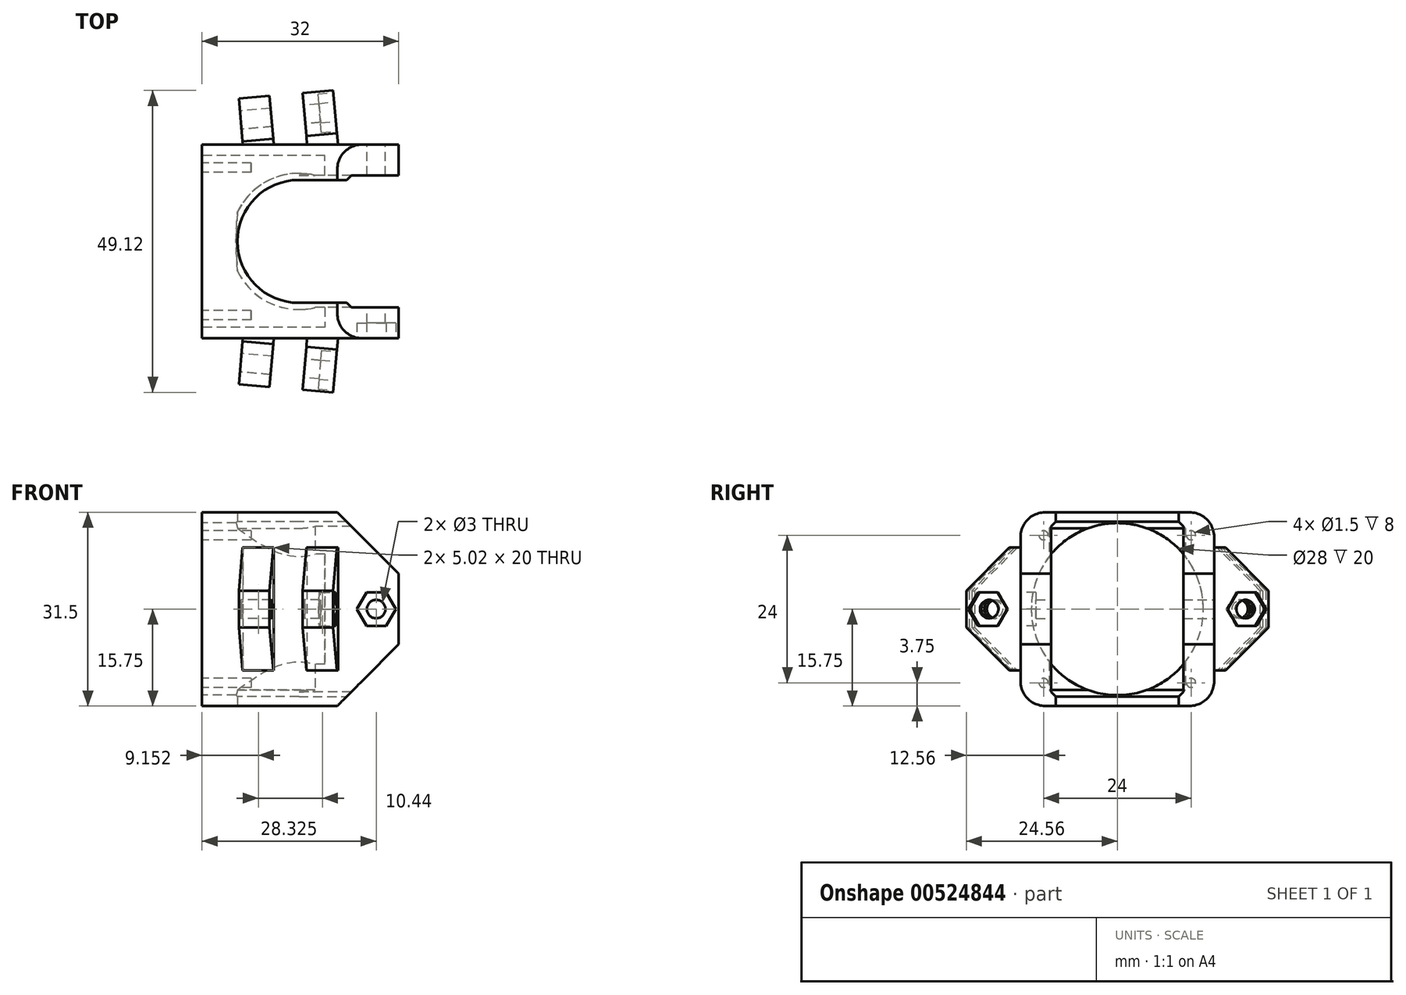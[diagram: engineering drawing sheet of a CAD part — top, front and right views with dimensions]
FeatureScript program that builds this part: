
annotation { "Feature Type Name" : "Feature", "Feature Type Description" : "" }
export const myFeature = defineFeature(function(context is Context, id is Id, definition is map)
    precondition{}
    {
        {
            var Q0;
            Q0=qCreatedBy(makeId("Top.planeOp"),FACE);
            var sketch = newSketch(context, id + "F0", { "sketchPlane" : qUnion([Q0])});
            skLineSegment(sketch, "E0.bottom", {"start": v(-15.75, 15.75) * mm, "end": v(16.25, 15.75) * mm});
            skLineSegment(sketch, "E0.top", {"start": v(-15.75, -15.75) * mm, "end": v(16.25, -15.75) * mm});
            skLineSegment(sketch, "E0.left", {"start": v(-15.75, 15.75) * mm, "end": v(-15.75, -15.75) * mm});
            skLineSegment(sketch, "E0.right", {"start": v(16.25, 15.75) * mm, "end": v(16.25, 10) * mm});
            skArc(sketch, "E1", {"start": v(0, 10) * mm, "mid": v(-10, 0) * mm, "end": v(0, -10) * mm});
            skLineSegment(sketch, "E2", {"start": v(16.25, 10) * mm, "end": v(0, 10) * mm});
            skLineSegment(sketch, "E3", {"start": v(16.25, -10) * mm, "end": v(0, -10) * mm});
            skLineSegment(sketch, "E4.trimOffspring", {"start": v(16.25, -10) * mm, "end": v(16.25, -15.75) * mm});
            skSolve(sketch);
        }
        {
            var Q0;
            Q0=makeQuery(id+"F0.imprint","IMPRINT",FACE,{"disambiguationData":[TD([[makeQuery(id+"F0.imprint","IMPRINT",EDGE,{"derivedFrom":sQuery(id+"F0.wireOp",EDGE,"E0.bottom")}),-1.0]])]});
            extrude(context, id + "F1", {"entities" : qUnion([Q0]), "depth" : (31.5 / 2) * mm, "offsetDistance" : 25 * mm, "hasSecondDirection" : true, "secondDirectionOppositeDirection" : true, "secondDirectionDepth" : (31.5 / 2) * mm});
        }
        {
            var Q0;
            Q0=makeQuery(id+"F1.opExtrude","CAP_EDGE",EDGE,{"disambiguationData":[OSD([sQuery(id+"F0.wireOp",EDGE,"E0.top")])],"isStart":false});
            fillet(context, id + "F2", {"entities" : qUnion([Q0]), "radius" : 4 * mm, "tangentPropagation" : true, "allowEdgeOverflow" : false});
        }
        {
            var Q0;
            Q0=makeQuery(id+"F1.opExtrude","CAP_EDGE",EDGE,{"disambiguationData":[OSD([sQuery(id+"F0.wireOp",EDGE,"E0.bottom")])],"isStart":false});
            fillet(context, id + "F3", {"entities" : qUnion([Q0]), "radius" : 4 * mm, "tangentPropagation" : true, "allowEdgeOverflow" : false});
        }
        {
            var Q0;
            Q0=makeQuery(id+"F1.opExtrude","CAP_EDGE",EDGE,{"disambiguationData":[OSD([sQuery(id+"F0.wireOp",EDGE,"E0.top")])],"isStart":true});
            fillet(context, id + "F4", {"entities" : qUnion([Q0]), "radius" : 4 * mm, "tangentPropagation" : true, "allowEdgeOverflow" : false});
        }
        {
            var Q0;
            Q0=makeQuery(id+"F1.opExtrude","CAP_EDGE",EDGE,{"disambiguationData":[OSD([sQuery(id+"F0.wireOp",EDGE,"E0.bottom")])],"isStart":true});
            fillet(context, id + "F5", {"entities" : qUnion([Q0]), "radius" : 4 * mm, "tangentPropagation" : true, "allowEdgeOverflow" : false});
        }
        {
            var Q0;
            Q0=qCreatedBy(makeId("Top.planeOp"),FACE);
            var sketch = newSketch(context, id + "F6", { "sketchPlane" : qUnion([Q0])});
            skArc(sketch, "E5", {"start": v(2.66, 10.75) * mm, "mid": v(-11.07, 0) * mm, "end": v(2.66, -10.75) * mm});
            skLineSegment(sketch, "E6", {"start": v(17, 10.75) * mm, "end": v(17, -10.75) * mm});
            skLineSegment(sketch, "E7", {"start": v(2.66, 10.75) * mm, "end": v(17, 10.75) * mm});
            skLineSegment(sketch, "E8", {"start": v(2.66, -10.75) * mm, "end": v(17, -10.75) * mm});
            skCircle(sketch, "E9", {"center": v(0, 0) * mm, "radius": 11.07 * mm, "construction": true});
            skSolve(sketch);
        }
        {
            var Q0;
            Q0 = qSketchRegion(id + "F6", true);
            extrude(context, id + "F7", {"entities" : qUnion([Q0]), "operationType" : NewBodyOperationType.REMOVE, "depth" : (26.3 / 2) * mm, "offsetDistance" : 25 * mm, "hasSecondDirection" : true, "secondDirectionOppositeDirection" : true, "secondDirectionDepth" : 13.15 * mm});
        }
        {
            var Q0;
            Q0=qCreatedBy(makeId("Front.planeOp"),FACE);
            var sketch = newSketch(context, id + "F8", { "sketchPlane" : qUnion([Q0])});
            skLineSegment(sketch, "E10", {"start": v(16.25, -5.75) * mm, "end": v(16.25, -15.75) * mm});
            skLineSegment(sketch, "E11", {"start": v(16.25, -15.75) * mm, "end": v(6.25, -15.75) * mm});
            skLineSegment(sketch, "E12", {"start": v(6.25, -15.75) * mm, "end": v(16.25, -5.75) * mm});
            skLineSegment(sketch, "E13", {"start": v(16.25, 5.75) * mm, "end": v(16.25, 15.75) * mm});
            skLineSegment(sketch, "E14", {"start": v(16.25, 15.75) * mm, "end": v(6.25, 15.75) * mm});
            skLineSegment(sketch, "E15", {"start": v(6.25, 15.75) * mm, "end": v(16.25, 5.75) * mm});
            skCircle(sketch, "E16", {"center": v(12.57, 0) * mm, "radius": 1.5 * mm});
            skSolve(sketch);
        }
        {
            var Q0;
            Q0 = qSketchRegion(id + "F8", true);
            extrude(context, id + "F9", {"entities" : qUnion([Q0]), "operationType" : NewBodyOperationType.REMOVE, "depth" : 16 * mm, "offsetDistance" : 25 * mm, "hasSecondDirection" : true, "secondDirectionOppositeDirection" : true, "secondDirectionDepth" : 16 * mm});
        }
        {
            var Q0;
            Q0=makeQuery(id+"F1.opExtrude","SWEPT_FACE",FACE,{"disambiguationData":[OSD([sQuery(id+"F0.wireOp",EDGE,"E0.left")])]});
            var sketch = newSketch(context, id + "F10", { "sketchPlane" : qUnion([Q0])});
            skCircle(sketch, "E17", {"center": v(0, 0) * mm, "radius": 14 * mm});
            skSolve(sketch);
        }
        {
            var Q0;
            Q0 = qSketchRegion(id + "F10", true);
            extrude(context, id + "F11", {"entities" : qUnion([Q0]), "operationType" : NewBodyOperationType.REMOVE, "oppositeDirection" : true, "depth" : 20 * mm, "offsetDistance" : 25 * mm});
        }
        {
            var Q0;
            Q0=makeQuery(id+"F1.opExtrude","SWEPT_FACE",FACE,{"disambiguationData":[OSD([sQuery(id+"F0.wireOp",EDGE,"E0.left")])]});
            var sketch = newSketch(context, id + "F12", { "sketchPlane" : qUnion([Q0])});
            skCircle(sketch, "E18", {"center": v(12, -12) * mm, "radius": 0.75 * mm});
            skCircle(sketch, "E19", {"center": v(-12, -12) * mm, "radius": 0.75 * mm});
            skCircle(sketch, "E20", {"center": v(-12, 12) * mm, "radius": 0.75 * mm});
            skCircle(sketch, "E21", {"center": v(12, 12) * mm, "radius": 0.75 * mm});
            skSolve(sketch);
        }
        {
            var Q0;
            Q0 = qSketchRegion(id + "F12", true);
            extrude(context, id + "F13", {"entities" : qUnion([Q0]), "operationType" : NewBodyOperationType.REMOVE, "oppositeDirection" : true, "depth" : (8) * mm, "offsetDistance" : 25 * mm});
        }
        {
            var Q0;
            Q0=makeQuery(id+"F7.boolean.opBoolean","INTERSECT",EDGE,{"derivedFrom":[makeQuery(id+"F1.opExtrude","SWEPT_FACE",FACE,{"disambiguationData":[OSD([sQuery(id+"F0.wireOp",EDGE,"E3")])]}),makeQuery(id+"F7.opExtrude","CAP_FACE",FACE,{"disambiguationData":[OSD([sQuery(id+"F6.wireOp",EDGE,"E5"),sQuery(id+"F6.wireOp",EDGE,"J0VfIJca-bOrv-LPtm-Diph-dnHVKdekmsFl"),sQuery(id+"F6.wireOp",EDGE,"DjFQ28n1-2k0m-8qY7-1Zac-zObu0h7Gc4Wb"),sQuery(id+"F6.wireOp",EDGE,"E6")])],"isStart":true})]});
            var Q1;
            {var subQ0=makeQuery(id+"F1.opExtrude","SWEPT_FACE",FACE,{"disambiguationData":[OSD([sQuery(id+"F0.wireOp",EDGE,"E1")])]});var subQ1=makeQuery(id+"F7.opExtrude","CAP_FACE",FACE,{"disambiguationData":[OSD([sQuery(id+"F6.wireOp",EDGE,"E5"),sQuery(id+"F6.wireOp",EDGE,"J0VfIJca-bOrv-LPtm-Diph-dnHVKdekmsFl"),sQuery(id+"F6.wireOp",EDGE,"DjFQ28n1-2k0m-8qY7-1Zac-zObu0h7Gc4Wb"),sQuery(id+"F6.wireOp",EDGE,"E6")])],"isStart":true});Q1=makeQuery(id+"F11.boolean.opBoolean","SPLIT",EDGE,{"disambiguationData":[TD([makeQuery(id+"F1.opExtrude","SWEPT_FACE",FACE,{"disambiguationData":[OSD([sQuery(id+"F0.wireOp",EDGE,"E3")])]})])],"derivedFrom":makeQuery(id+"F7.boolean.opBoolean","INTERSECT",EDGE,{"derivedFrom":[subQ0,subQ1]})});}
            chamfer(context, id + "F14", {"entities" : qUnion([Q0, Q1]), "width" : 1.07 * mm, "tangentPropagation" : true});
        }
        {
            var Q0;
            Q0=makeQuery(id+"F7.boolean.opBoolean","INTERSECT",EDGE,{"derivedFrom":[makeQuery(id+"F1.opExtrude","SWEPT_FACE",FACE,{"disambiguationData":[OSD([sQuery(id+"F0.wireOp",EDGE,"E2")])]}),makeQuery(id+"F7.opExtrude","CAP_FACE",FACE,{"disambiguationData":[OSD([sQuery(id+"F6.wireOp",EDGE,"E5"),sQuery(id+"F6.wireOp",EDGE,"J0VfIJca-bOrv-LPtm-Diph-dnHVKdekmsFl"),sQuery(id+"F6.wireOp",EDGE,"DjFQ28n1-2k0m-8qY7-1Zac-zObu0h7Gc4Wb"),sQuery(id+"F6.wireOp",EDGE,"E6")])],"isStart":true})]});
            chamfer(context, id + "F15", {"entities" : qUnion([Q0]), "width" : 1.07 * mm, "tangentPropagation" : true});
        }
        {
            var Q0;
            Q0=makeQuery(id+"F7.boolean.opBoolean","INTERSECT",EDGE,{"derivedFrom":[makeQuery(id+"F1.opExtrude","SWEPT_FACE",FACE,{"disambiguationData":[OSD([sQuery(id+"F0.wireOp",EDGE,"E2")])]}),makeQuery(id+"F7.opExtrude","CAP_FACE",FACE,{"disambiguationData":[OSD([sQuery(id+"F6.wireOp",EDGE,"E5"),sQuery(id+"F6.wireOp",EDGE,"J0VfIJca-bOrv-LPtm-Diph-dnHVKdekmsFl"),sQuery(id+"F6.wireOp",EDGE,"DjFQ28n1-2k0m-8qY7-1Zac-zObu0h7Gc4Wb"),sQuery(id+"F6.wireOp",EDGE,"E6")])],"isStart":false})]});
            var Q1;
            {var subQ0=makeQuery(id+"F1.opExtrude","SWEPT_FACE",FACE,{"disambiguationData":[OSD([sQuery(id+"F0.wireOp",EDGE,"E1")])]});var subQ1=makeQuery(id+"F7.opExtrude","CAP_FACE",FACE,{"disambiguationData":[OSD([sQuery(id+"F6.wireOp",EDGE,"E5"),sQuery(id+"F6.wireOp",EDGE,"J0VfIJca-bOrv-LPtm-Diph-dnHVKdekmsFl"),sQuery(id+"F6.wireOp",EDGE,"DjFQ28n1-2k0m-8qY7-1Zac-zObu0h7Gc4Wb"),sQuery(id+"F6.wireOp",EDGE,"E6")])],"isStart":false});Q1=makeQuery(id+"F11.boolean.opBoolean","SPLIT",EDGE,{"disambiguationData":[TD([makeQuery(id+"F1.opExtrude","SWEPT_FACE",FACE,{"disambiguationData":[OSD([sQuery(id+"F0.wireOp",EDGE,"E2")])]})])],"derivedFrom":makeQuery(id+"F7.boolean.opBoolean","INTERSECT",EDGE,{"derivedFrom":[subQ0,subQ1]})});}
            var Q2;
            {var subQ0=makeQuery(id+"F1.opExtrude","SWEPT_FACE",FACE,{"disambiguationData":[OSD([sQuery(id+"F0.wireOp",EDGE,"E1")])]});var subQ1=makeQuery(id+"F7.opExtrude","CAP_FACE",FACE,{"disambiguationData":[OSD([sQuery(id+"F6.wireOp",EDGE,"E5"),sQuery(id+"F6.wireOp",EDGE,"J0VfIJca-bOrv-LPtm-Diph-dnHVKdekmsFl"),sQuery(id+"F6.wireOp",EDGE,"DjFQ28n1-2k0m-8qY7-1Zac-zObu0h7Gc4Wb"),sQuery(id+"F6.wireOp",EDGE,"E6")])],"isStart":false});Q2=makeQuery(id+"F11.boolean.opBoolean","SPLIT",EDGE,{"disambiguationData":[TD([makeQuery(id+"F1.opExtrude","SWEPT_FACE",FACE,{"disambiguationData":[OSD([sQuery(id+"F0.wireOp",EDGE,"E3")])]})])],"derivedFrom":makeQuery(id+"F7.boolean.opBoolean","INTERSECT",EDGE,{"derivedFrom":[subQ0,subQ1]})});}
            var Q3;
            Q3=makeQuery(id+"F7.boolean.opBoolean","INTERSECT",EDGE,{"derivedFrom":[makeQuery(id+"F1.opExtrude","SWEPT_FACE",FACE,{"disambiguationData":[OSD([sQuery(id+"F0.wireOp",EDGE,"E3")])]}),makeQuery(id+"F7.opExtrude","CAP_FACE",FACE,{"disambiguationData":[OSD([sQuery(id+"F6.wireOp",EDGE,"E5"),sQuery(id+"F6.wireOp",EDGE,"J0VfIJca-bOrv-LPtm-Diph-dnHVKdekmsFl"),sQuery(id+"F6.wireOp",EDGE,"DjFQ28n1-2k0m-8qY7-1Zac-zObu0h7Gc4Wb"),sQuery(id+"F6.wireOp",EDGE,"E6")])],"isStart":false})]});
            chamfer(context, id + "F16", {"entities" : qUnion([Q0, Q1, Q2, Q3]), "width" : 1.07 * mm, "tangentPropagation" : true});
        }
        {
            var Q0;
            Q0=qCreatedBy(makeId("Top.planeOp"),FACE);
            var sketch = newSketch(context, id + "F17", { "sketchPlane" : qUnion([Q0])});
            skLineSegment(sketch, "E22", {"start": v(-4.09, 15.75) * mm, "end": v(-4.78, 23.66) * mm});
            skLineSegment(sketch, "E23", {"start": v(-4.78, 23.66) * mm, "end": v(-9.76, 23.22) * mm});
            skLineSegment(sketch, "E24", {"start": v(-9.76, 23.22) * mm, "end": v(-9.1, 15.75) * mm});
            skLineSegment(sketch, "E25", {"start": v(-9.1, 15.75) * mm, "end": v(-4.09, 15.75) * mm});
            skLineSegment(sketch, "E26", {"start": v(0, 0) * mm, "end": v(-3.21, 36.74) * mm, "construction": true});
            skLineSegment(sketch, "E27", {"start": v(1.33, 15.75) * mm, "end": v(0.6, 24.13) * mm});
            skLineSegment(sketch, "E28", {"start": v(0.6, 24.13) * mm, "end": v(5.58, 24.56) * mm});
            skLineSegment(sketch, "E29", {"start": v(5.58, 24.56) * mm, "end": v(6.35, 15.75) * mm});
            skLineSegment(sketch, "E30", {"start": v(6.35, 15.75) * mm, "end": v(1.33, 15.75) * mm});
            skLineSegment(sketch, "E31", {"start": v(0, 0) * mm, "end": v(-3.36, -38.35) * mm, "construction": true});
            skLineSegment(sketch, "E32", {"start": v(-9.1, -15.75) * mm, "end": v(-9.76, -23.22) * mm});
            skLineSegment(sketch, "E33", {"start": v(-9.76, -23.22) * mm, "end": v(-4.78, -23.66) * mm});
            skLineSegment(sketch, "E34", {"start": v(-4.78, -23.66) * mm, "end": v(-4.09, -15.75) * mm});
            skLineSegment(sketch, "E35", {"start": v(-4.09, -15.75) * mm, "end": v(-9.1, -15.75) * mm});
            skLineSegment(sketch, "E36", {"start": v(1.33, -15.75) * mm, "end": v(0.6, -24.13) * mm});
            skLineSegment(sketch, "E37", {"start": v(0.6, -24.13) * mm, "end": v(5.58, -24.56) * mm});
            skLineSegment(sketch, "E38", {"start": v(5.58, -24.56) * mm, "end": v(6.35, -15.75) * mm});
            skLineSegment(sketch, "E39", {"start": v(6.35, -15.75) * mm, "end": v(1.33, -15.75) * mm});
            skSolve(sketch);
        }
        {
            var Q0;
            Q0 = qSketchRegion(id + "F17", true);
            extrude(context, id + "F18", {"entities" : qUnion([Q0]), "operationType" : NewBodyOperationType.ADD, "depth" : 10 * mm, "offsetDistance" : 25 * mm, "hasSecondDirection" : true, "secondDirectionOppositeDirection" : true, "secondDirectionDepth" : 10 * mm});
        }
        {
            var Q0;
            Q0=makeQuery(id+"F18.opExtrude","SWEPT_FACE",FACE,{"disambiguationData":[OSD([sQuery(id+"F17.wireOp",EDGE,"E24")])]});
            var sketch = newSketch(context, id + "F19", { "sketchPlane" : qUnion([Q0])});
            skLineSegment(sketch, "E40", {"start": v(-23.98, 3) * mm, "end": v(-16.98, 10) * mm});
            skLineSegment(sketch, "E41", {"start": v(-16.98, 10) * mm, "end": v(-23.98, 10) * mm});
            skLineSegment(sketch, "E42", {"start": v(-23.98, 10) * mm, "end": v(-23.98, 3) * mm});
            skLineSegment(sketch, "E43", {"start": v(-23.98, -3) * mm, "end": v(-16.98, -10) * mm});
            skLineSegment(sketch, "E44", {"start": v(-16.98, -10) * mm, "end": v(-23.98, -10) * mm});
            skLineSegment(sketch, "E45", {"start": v(-23.98, -10) * mm, "end": v(-23.98, -3) * mm});
            skCircle(sketch, "E46", {"center": v(-20.48, 0) * mm, "radius": 1.5 * mm});
            skSolve(sketch);
        }
        {
            var Q0;
            Q0 = qSketchRegion(id + "F19", true);
            extrude(context, id + "F20", {"entities" : qUnion([Q0]), "operationType" : NewBodyOperationType.REMOVE, "oppositeDirection" : true, "depth" : 25 * mm, "offsetDistance" : 25 * mm});
        }
        {
            var Q0;
            Q0=makeQuery(id+"F18.opExtrude","SWEPT_FACE",FACE,{"disambiguationData":[OSD([sQuery(id+"F17.wireOp",EDGE,"E32")])]});
            var sketch = newSketch(context, id + "F21", { "sketchPlane" : qUnion([Q0])});
            skLineSegment(sketch, "E47", {"start": v(16.98, 10) * mm, "end": v(23.98, 3) * mm});
            skLineSegment(sketch, "E48", {"start": v(23.98, 3) * mm, "end": v(23.98, 10) * mm});
            skLineSegment(sketch, "E49", {"start": v(23.98, 10) * mm, "end": v(16.98, 10) * mm});
            skLineSegment(sketch, "E50", {"start": v(23.98, -3) * mm, "end": v(16.98, -10) * mm});
            skLineSegment(sketch, "E51", {"start": v(16.98, -10) * mm, "end": v(23.98, -10) * mm});
            skLineSegment(sketch, "E52", {"start": v(23.98, -10) * mm, "end": v(23.98, -3) * mm});
            skCircle(sketch, "E53", {"center": v(20.48, 0) * mm, "radius": 1.5 * mm});
            skSolve(sketch);
        }
        {
            var Q0;
            Q0 = qSketchRegion(id + "F21", true);
            extrude(context, id + "F22", {"entities" : qUnion([Q0]), "operationType" : NewBodyOperationType.REMOVE, "oppositeDirection" : true, "depth" : 25 * mm, "offsetDistance" : 25 * mm});
        }
        {
            var Q0;
            Q0=makeQuery(id+"F1.opExtrude","SWEPT_FACE",FACE,{"disambiguationData":[OSD([sQuery(id+"F0.wireOp",EDGE,"E0.top")])]});
            var sketch = newSketch(context, id + "F23", { "sketchPlane" : qUnion([Q0])});
            skLineSegment(sketch, "E54", {"start": v(14.16, -2.75) * mm, "end": v(10.99, -2.75) * mm});
            skLineSegment(sketch, "E55", {"start": v(10.99, -2.75) * mm, "end": v(9.4, 0) * mm});
            skLineSegment(sketch, "E56", {"start": v(9.4, 0) * mm, "end": v(10.99, 2.75) * mm});
            skLineSegment(sketch, "E57", {"start": v(10.99, 2.75) * mm, "end": v(14.16, 2.75) * mm});
            skLineSegment(sketch, "E58", {"start": v(14.16, 2.75) * mm, "end": v(15.75, 0) * mm});
            skLineSegment(sketch, "E59", {"start": v(15.75, 0) * mm, "end": v(14.16, -2.75) * mm});
            skCircle(sketch, "E60", {"center": v(12.57, 0) * mm, "radius": 2.75 * mm, "construction": true});
            skSolve(sketch);
        }
        {
            var Q0;
            Q0 = qSketchRegion(id + "F23", true);
            extrude(context, id + "F24", {"entities" : qUnion([Q0]), "operationType" : NewBodyOperationType.REMOVE, "oppositeDirection" : true, "depth" : 2.5 * mm, "offsetDistance" : 25 * mm});
        }
        {
            var Q0;
            Q0=makeQuery(id+"F18.opExtrude","SWEPT_FACE",FACE,{"disambiguationData":[OSD([sQuery(id+"F17.wireOp",EDGE,"E38")])]});
            var sketch = newSketch(context, id + "F25", { "sketchPlane" : qUnion([Q0])});
            skCircle(sketch, "E61", {"center": v(-20.48, 0) * mm, "radius": 2.75 * mm, "construction": true});
            skLineSegment(sketch, "E62", {"start": v(-18.9, 2.75) * mm, "end": v(-22.07, 2.75) * mm});
            skLineSegment(sketch, "E63", {"start": v(-22.07, 2.75) * mm, "end": v(-23.66, 0) * mm});
            skLineSegment(sketch, "E64", {"start": v(-23.66, 0) * mm, "end": v(-22.07, -2.75) * mm});
            skLineSegment(sketch, "E65", {"start": v(-22.07, -2.75) * mm, "end": v(-18.9, -2.75) * mm});
            skLineSegment(sketch, "E66", {"start": v(-18.9, -2.75) * mm, "end": v(-17.3, 0) * mm});
            skLineSegment(sketch, "E67", {"start": v(-17.3, 0) * mm, "end": v(-18.9, 2.75) * mm});
            skSolve(sketch);
        }
        {
            var Q0;
            Q0 = qSketchRegion(id + "F25", true);
            extrude(context, id + "F26", {"entities" : qUnion([Q0]), "operationType" : NewBodyOperationType.REMOVE, "oppositeDirection" : true, "depth" : 2.5 * mm, "offsetDistance" : 25 * mm});
        }
        {
            var Q0;
            Q0=makeQuery(id+"F18.opExtrude","SWEPT_FACE",FACE,{"disambiguationData":[OSD([sQuery(id+"F17.wireOp",EDGE,"E29")])]});
            var sketch = newSketch(context, id + "F27", { "sketchPlane" : qUnion([Q0])});
            skCircle(sketch, "E68", {"center": v(20.48, 0) * mm, "radius": 2.75 * mm, "construction": true});
            skLineSegment(sketch, "E69", {"start": v(18.9, -2.75) * mm, "end": v(22.07, -2.75) * mm});
            skLineSegment(sketch, "E70", {"start": v(22.07, -2.75) * mm, "end": v(23.66, 0) * mm});
            skLineSegment(sketch, "E71", {"start": v(23.66, 0) * mm, "end": v(22.07, 2.75) * mm});
            skLineSegment(sketch, "E72", {"start": v(22.07, 2.75) * mm, "end": v(18.9, 2.75) * mm});
            skLineSegment(sketch, "E73", {"start": v(18.9, 2.75) * mm, "end": v(17.3, 0) * mm});
            skLineSegment(sketch, "E74", {"start": v(17.3, 0) * mm, "end": v(18.9, -2.75) * mm});
            skSolve(sketch);
        }
        {
            var Q0;
            Q0 = qSketchRegion(id + "F27", true);
            extrude(context, id + "F28", {"entities" : qUnion([Q0]), "operationType" : NewBodyOperationType.REMOVE, "oppositeDirection" : true, "depth" : 2.5 * mm, "offsetDistance" : 25 * mm});
        }
    });
